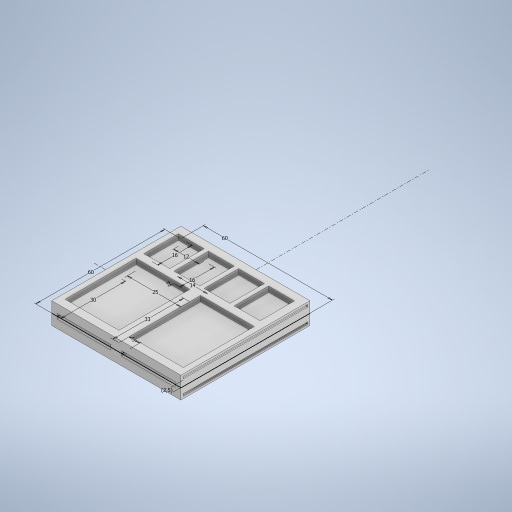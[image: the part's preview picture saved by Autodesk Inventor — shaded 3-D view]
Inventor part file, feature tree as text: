
AUTODESK INVENTOR PART (.ipt)
format: ipt  version: 2023 (Build 270158000, 158)  size: 448,000 bytes
history: native  units: mm
features: extrude x10, sketch x3
ambient origin geometry x8: Origin, YZ Plane, XZ Plane, XY Plane, X Axis, Y Axis, Z Axis, Center Point
bodies: Solido1 (feature_tree)
feature tree (13):
  sketch  "Schizzo1"
  extrude  "Estrusione1"  Depth=25.0mm
  extrude  "Estrusione2"  Depth=33.0mm
  extrude  "Estrusione10"  Depth=12.0mm
  extrude  "Estrusione11"  Depth=60.0mm
  extrude  "Estrusione12"  Depth=10.0mm TaperAngle=0.0deg
  extrude  "Estrusione13"  Depth=5.0mm TaperAngle=0.0deg
  sketch  "Schizzo5"
  extrude  "Estrusione14"  Depth=30.0mm
  extrude  "Estrusione15"  Depth=16.0mm
  sketch  "Schizzo8"
  extrude  "Estrusione16"  Depth=60.0mm
  extrude  "Estrusione17"  Depth=2.0mm
